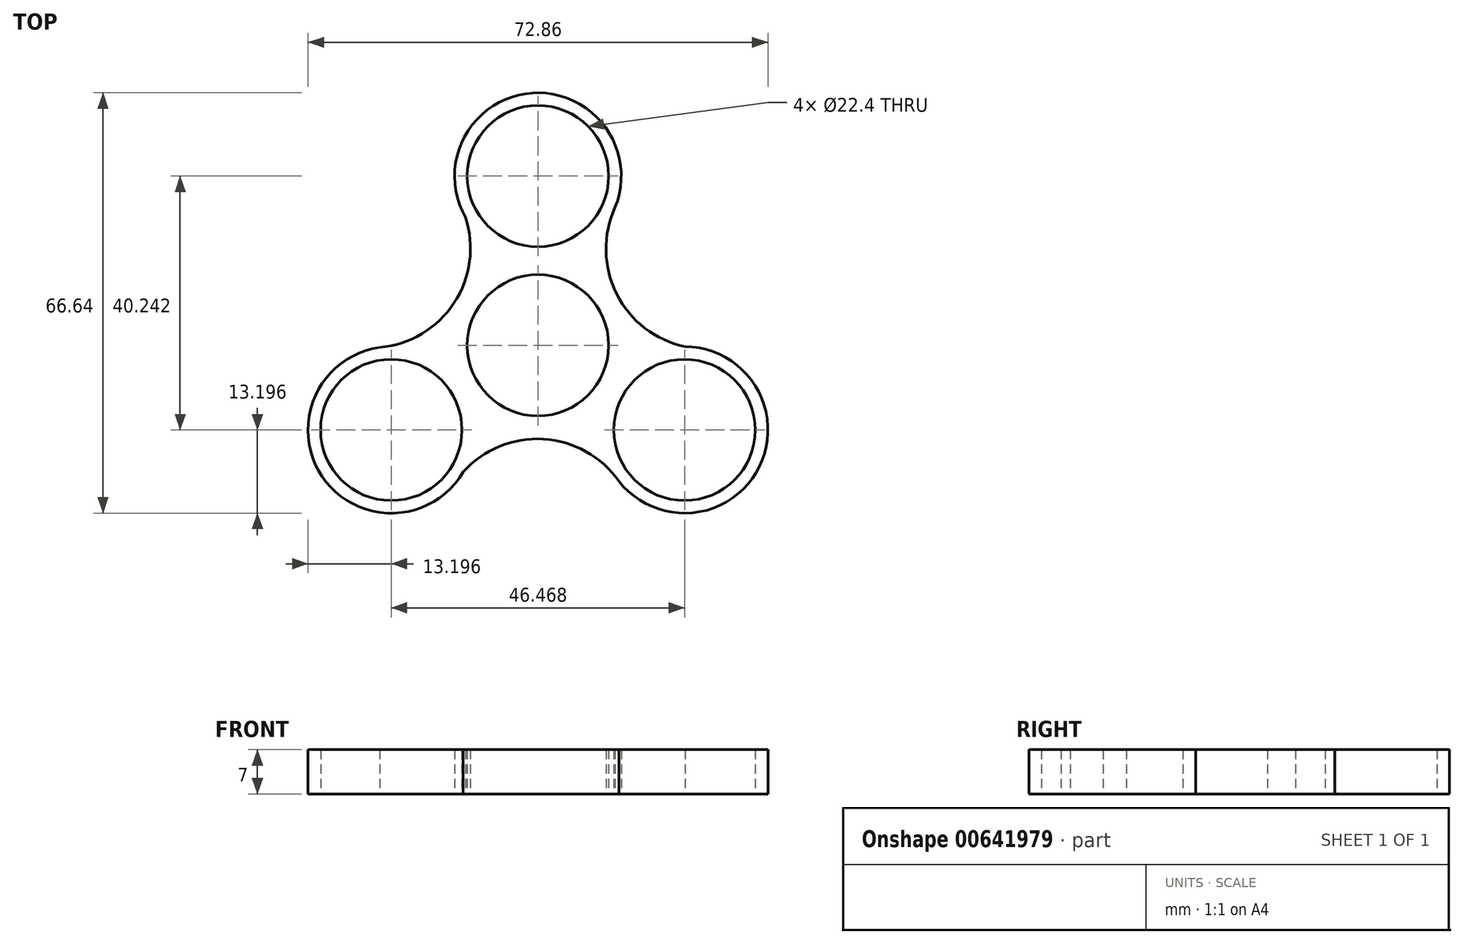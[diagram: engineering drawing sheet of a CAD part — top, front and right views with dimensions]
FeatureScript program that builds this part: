
annotation { "Feature Type Name" : "Feature", "Feature Type Description" : "" }
export const myFeature = defineFeature(function(context is Context, id is Id, definition is map)
    precondition{}
    {
        {
            var Q0;
            Q0=qCreatedBy(makeId("Top.planeOp"),FACE);
            var sketch = newSketch(context, id + "F0", { "sketchPlane" : qUnion([Q0])});
            skCircle(sketch, "E0", {"center": v(0, 0) * mm, "radius": 11.2 * mm});
            skCircle(sketch, "E1", {"center": v(0, 26.83) * mm, "radius": 11.2 * mm});
            skArc(sketch, "E2", {"start": v(11.96, 21.24) * mm, "mid": v(-0.53, 40.02) * mm, "end": v(-11.47, 20.3) * mm});
            skCircle(sketch, "E3.1.0", {"center": v(-23.23, -13.41) * mm, "radius": 11.2 * mm});
            skArc(sketch, "E3.1.1", {"start": v(-24.38, -0.26) * mm, "mid": v(-34.39, -20.47) * mm, "end": v(-11.84, -20.08) * mm});
            skCircle(sketch, "E3.2.0", {"center": v(23.23, -13.41) * mm, "radius": 11.2 * mm});
            skArc(sketch, "E3.2.1", {"start": v(12.42, -20.98) * mm, "mid": v(34.92, -19.55) * mm, "end": v(23.3, -0.21) * mm});
            skArc(sketch, "E4", {"start": v(12.23, 21.87) * mm, "mid": v(12.45, 8.16) * mm, "end": v(23.3, -0.21) * mm});
            skArc(sketch, "E5.1.0", {"start": v(-25.06, -0.34) * mm, "mid": v(-13.3, 6.7) * mm, "end": v(-11.47, 20.3) * mm});
            skArc(sketch, "E5.2.0", {"start": v(12.82, -21.53) * mm, "mid": v(0.84, -14.87) * mm, "end": v(-11.84, -20.08) * mm});
            skSolve(sketch);
        }
        {
            var Q0;
            Q0=makeQuery(id+"F0.imprint","IMPRINT",FACE,{"disambiguationData":[TD([[makeQuery(id+"F0.imprint","IMPRINT",EDGE,{"derivedFrom":sQuery(id+"F0.wireOp",EDGE,"E0")}),-1.0]])]});
            extrude(context, id + "F1", {"entities" : qUnion([Q0]), "depth" : 7 * mm, "offsetDistance" : 25 * mm});
        }
    });
